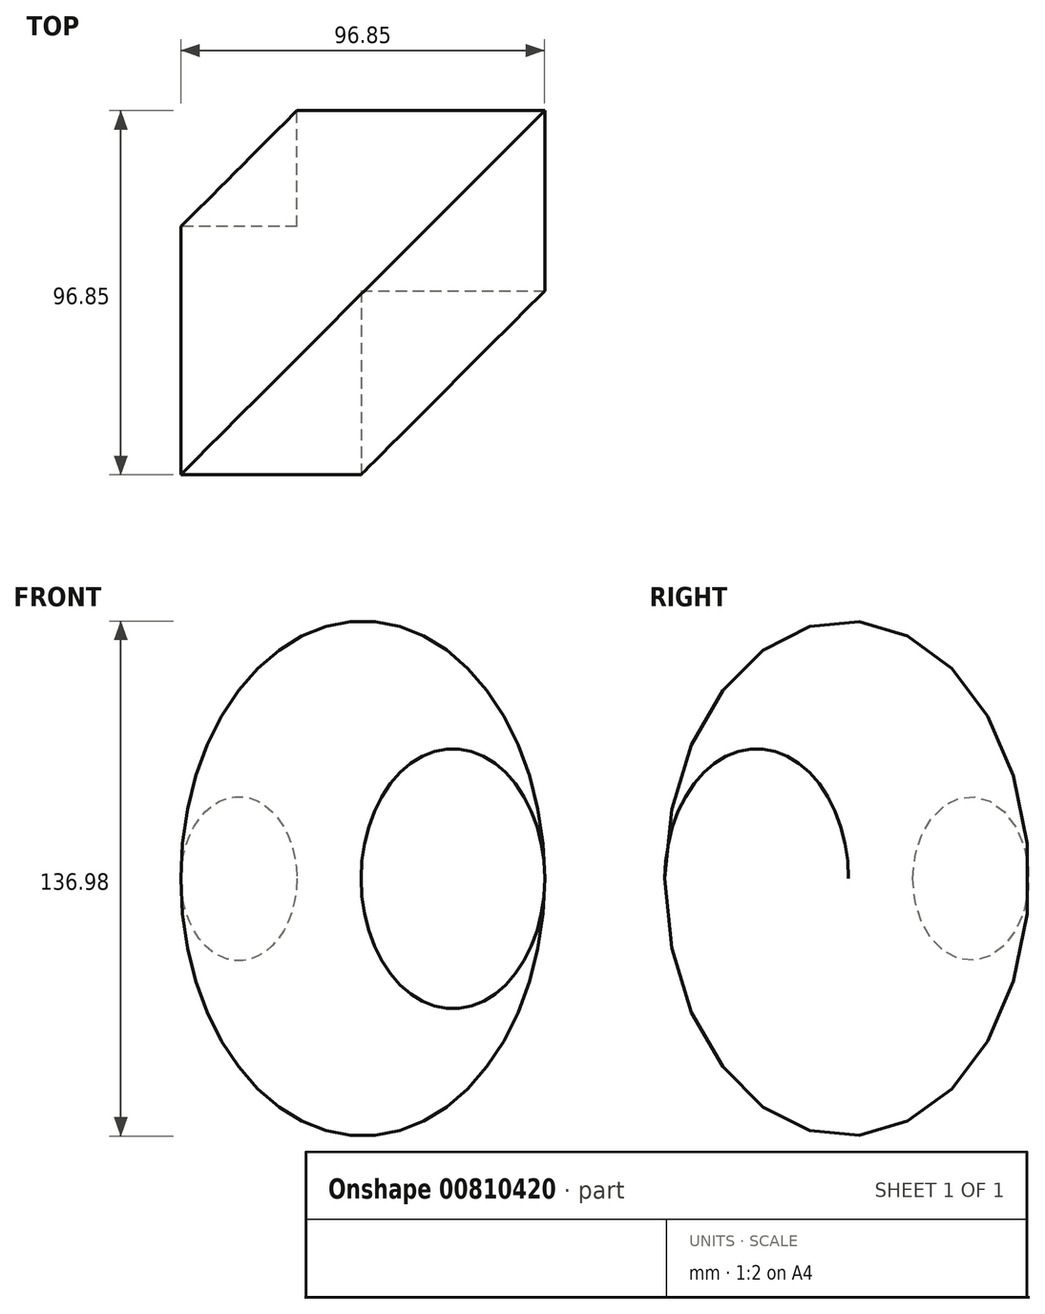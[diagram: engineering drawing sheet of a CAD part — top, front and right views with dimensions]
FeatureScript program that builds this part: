
annotation { "Feature Type Name" : "Feature", "Feature Type Description" : "" }
export const myFeature = defineFeature(function(context is Context, id is Id, definition is map)
    precondition{}
    {
        {
            var Q0;
            Q0=qCreatedBy(makeId("Top.planeOp"),FACE);
            var sketch = newSketch(context, id + "F0", { "sketchPlane" : qUnion([Q0])});
            skLineSegment(sketch, "E0.bottom", {"start": v(-23.98, 47.48) * mm, "end": v(23.99, 47.48) * mm});
            skLineSegment(sketch, "E0.top", {"start": v(-23.98, -18.51) * mm, "end": v(23.99, -18.51) * mm});
            skLineSegment(sketch, "E0.left", {"start": v(-23.98, 47.48) * mm, "end": v(-23.98, -18.51) * mm});
            skLineSegment(sketch, "E0.right", {"start": v(23.99, 47.48) * mm, "end": v(23.99, -18.51) * mm});
            skLineSegment(sketch, "E1", {"start": v(-7.48, 61.84) * mm, "end": v(38.96, 15.4) * mm});
            skSolve(sketch);
        }
        {
            var Q0;
            {var subQ1=sQuery(id+"F0.wireOp",EDGE,"E0.top");Q0=makeQuery(id+"F0.imprint","IMPRINT",FACE,{"disambiguationData":[TD([[makeQuery(id+"F0.imprint","IMPRINT",EDGE,{"derivedFrom":subQ1}),1.0]])]});}
            var Q1;
            Q1=sQuery(id+"F0.wireOp",EDGE,"E1");
            revolve(context, id + "F1", {"surfaceOperationType" : NewSurfaceOperationType.NEW, "entities" : qUnion([Q0]), "axis" : qUnion([Q1]), "revolveType" : RevolveType.FULL});
        }
    });
